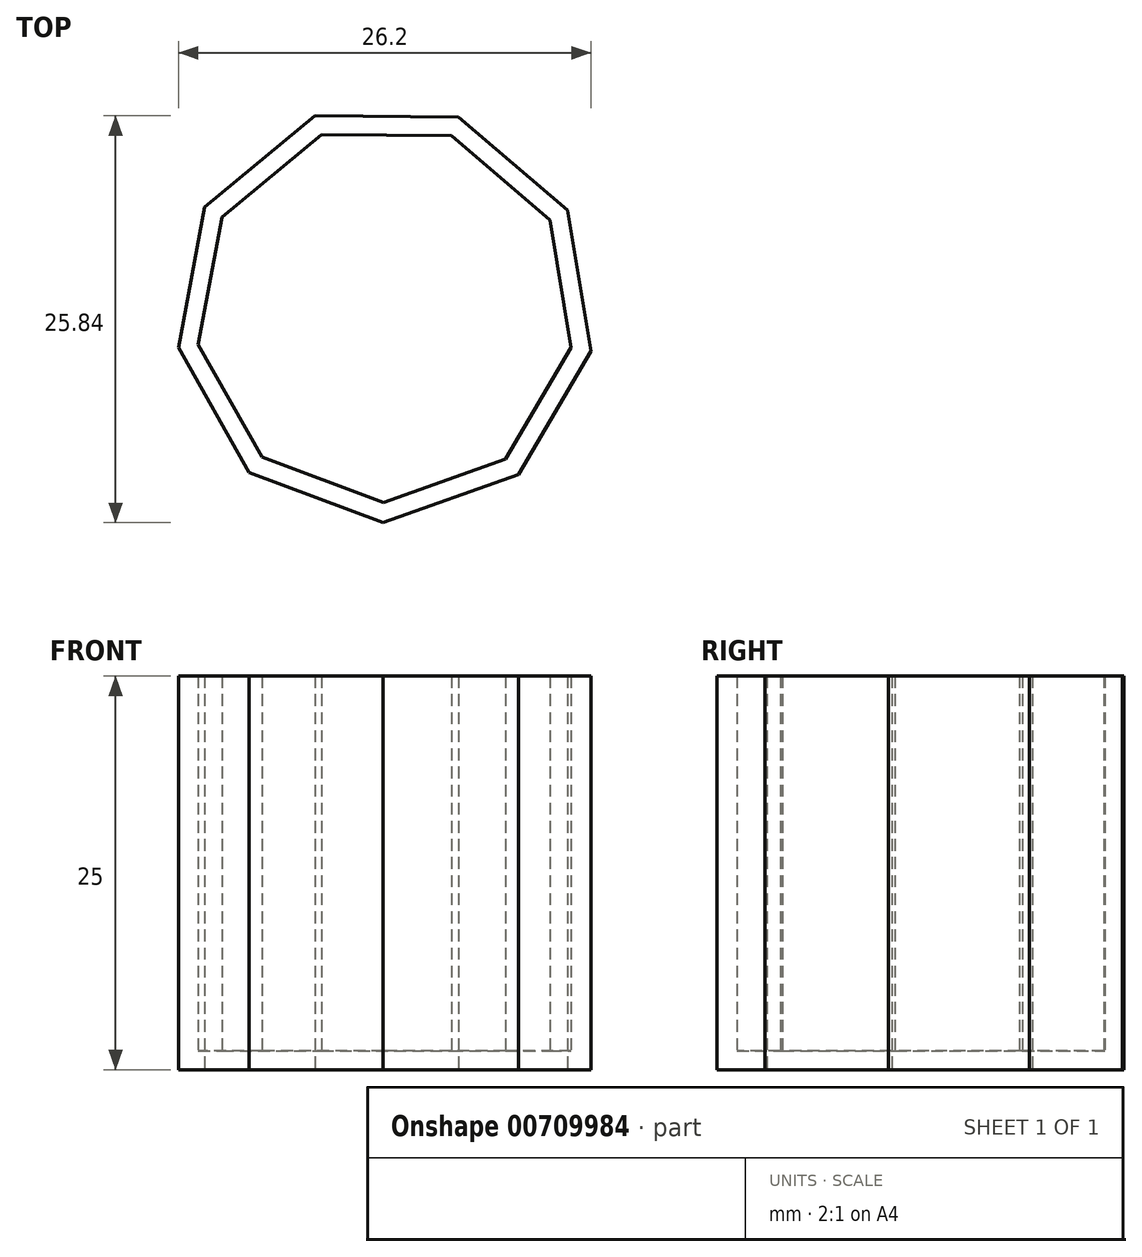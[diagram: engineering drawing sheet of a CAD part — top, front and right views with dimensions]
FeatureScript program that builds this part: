
annotation { "Feature Type Name" : "Feature", "Feature Type Description" : "" }
export const myFeature = defineFeature(function(context is Context, id is Id, definition is map)
    precondition{}
    {
        {
            var Q0;
            Q0=qCreatedBy(makeId("Top.planeOp"),FACE);
            var sketch = newSketch(context, id + "F0", { "sketchPlane" : qUnion([Q0])});
            skCircle(sketch, "E0.cCircle", {"center": v(0, 0) * mm, "radius": 12.5 * mm, "construction": true});
            skLineSegment(sketch, "E0.0", {"start": v(13.08, -2.42) * mm, "end": v(8.46, -10.26) * mm});
            skLineSegment(sketch, "E0.1", {"start": v(8.46, -10.26) * mm, "end": v(-0.11, -13.3) * mm});
            skLineSegment(sketch, "E0.2", {"start": v(-0.11, -13.3) * mm, "end": v(-8.64, -10.12) * mm});
            skLineSegment(sketch, "E0.3", {"start": v(-8.64, -10.12) * mm, "end": v(-13.12, -2.2) * mm});
            skLineSegment(sketch, "E0.4", {"start": v(-13.12, -2.2) * mm, "end": v(-11.46, 6.75) * mm});
            skLineSegment(sketch, "E0.5", {"start": v(-11.46, 6.75) * mm, "end": v(-4.44, 12.54) * mm});
            skLineSegment(sketch, "E0.6", {"start": v(-4.44, 12.54) * mm, "end": v(4.66, 12.46) * mm});
            skLineSegment(sketch, "E0.7", {"start": v(4.66, 12.46) * mm, "end": v(11.58, 6.55) * mm});
            skLineSegment(sketch, "E0.8", {"start": v(11.58, 6.55) * mm, "end": v(13.08, -2.42) * mm});
            skPoint(sketch, "E0.0.midPoint", {"position": v(10.77, -6.34) * mm});
            skSolve(sketch);
        }
        {
            var Q0;
            Q0=makeQuery(id+"F0.imprint","IMPRINT",FACE,{"disambiguationData":[TD([[makeQuery(id+"F0.imprint","IMPRINT",EDGE,{"derivedFrom":sQuery(id+"F0.wireOp",EDGE,"E0.0")}),-1.0]])]});
            extrude(context, id + "F1", {"entities" : qUnion([Q0]), "depth" : 25 * mm, "offsetDistance" : 25 * mm});
        }
        {
            var Q0;
            Q0=makeQuery(id+"F1.opExtrude","CAP_FACE",FACE,{"disambiguationData":[OSD([sQuery(id+"F0.wireOp",EDGE,"E0.0"),sQuery(id+"F0.wireOp",EDGE,"E0.1"),sQuery(id+"F0.wireOp",EDGE,"E0.2"),sQuery(id+"F0.wireOp",EDGE,"E0.3"),sQuery(id+"F0.wireOp",EDGE,"E0.4"),sQuery(id+"F0.wireOp",EDGE,"E0.5"),sQuery(id+"F0.wireOp",EDGE,"E0.6"),sQuery(id+"F0.wireOp",EDGE,"E0.7"),sQuery(id+"F0.wireOp",EDGE,"E0.8")])],"isStart":false});
            shell(context, id + "F2", {"entities" : qUnion([Q0]), "thickness" : 1.2 * mm});
        }
    });
